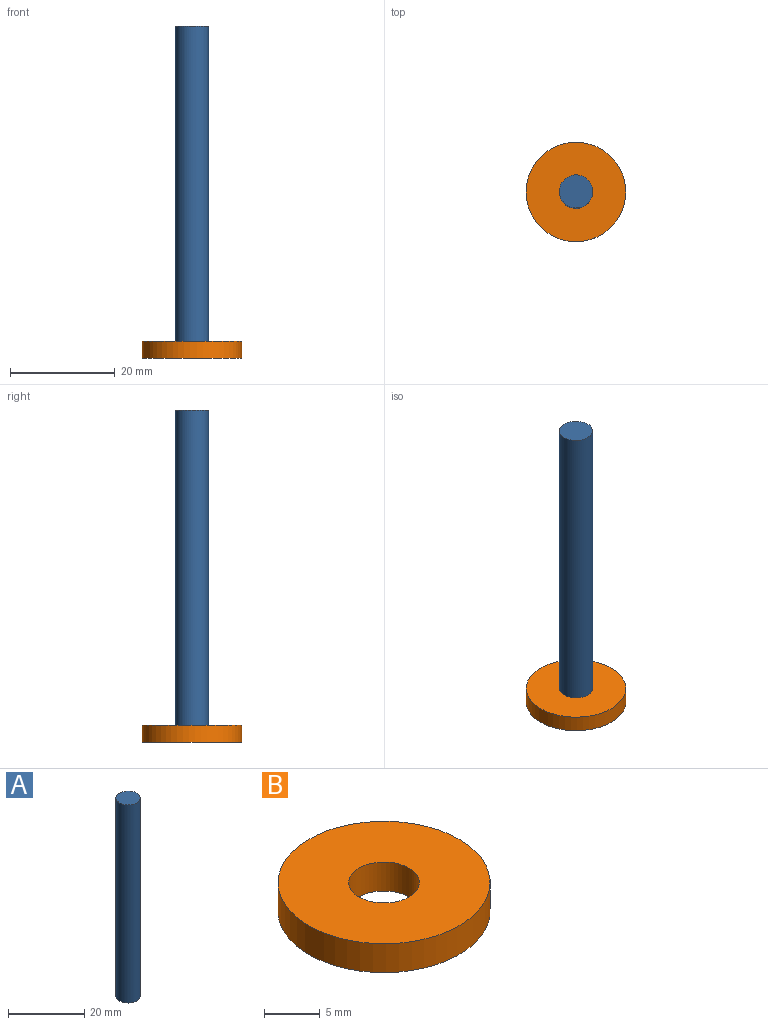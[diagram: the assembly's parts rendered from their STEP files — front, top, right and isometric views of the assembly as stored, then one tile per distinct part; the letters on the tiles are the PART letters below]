
ASSEMBLY  parts=2 mates=1
PART A: 3 faces, bbox 6.4x6.4x63.5 mm
  f0: plane 6.35x6.35mm, normal (0,0,1), area 31.7mm2, adj f1
  f1: cylinder r=3.17mm len=63.5mm, axis (0,0,-1), area 1266.8mm2, adj f0,f2
  f2: plane 6.35x6.35mm, normal (0,0,-1), area 31.7mm2, adj f1
PART B: 4 faces, bbox 19.1x19.1x3.2 mm
  f0: cylinder r=3.17mm len=6.35mm, axis (0,0,-1), area 63.3mm2, adj f2,f3
  f1: cylinder r=9.53mm len=19.05mm, axis (0,0,-1), area 190mm2, adj f2,f3
  f2: plane 19.05x19.05mm, normal (0,0,1), area 253.4mm2, adj f0,f1
  f3: plane 19.05x19.05mm, normal (0,0,-1), area 253.4mm2, adj f0,f1
PLACE A t=(69.85,0,-66.68)mm
PLACE B t=(69.85,0,-66.68)mm
MATE fastened A.f1 <-> B.f0  axis (0,0,-1) through (0,0,-3.17)mm
